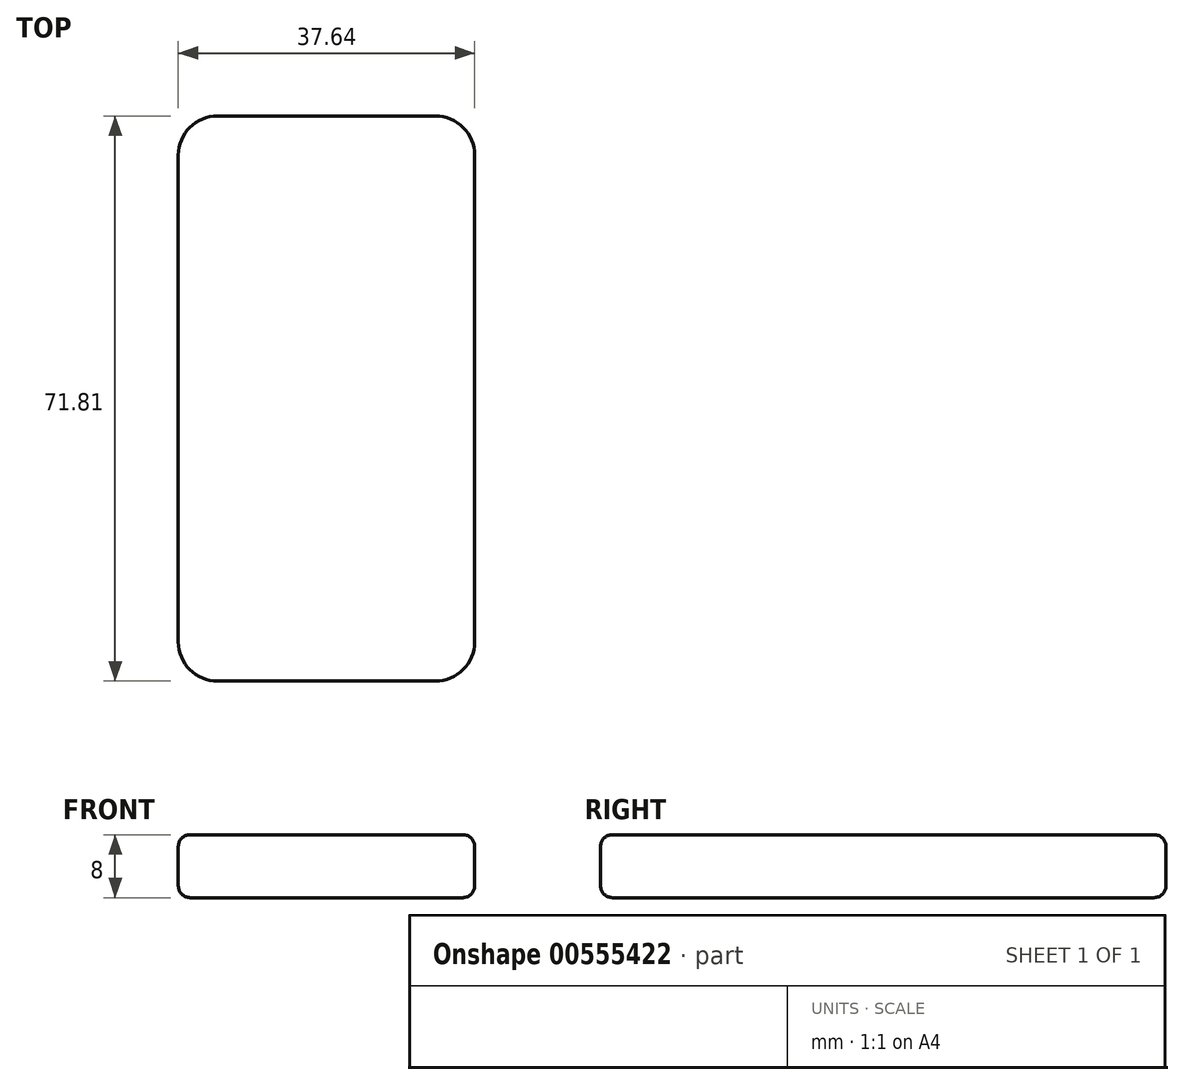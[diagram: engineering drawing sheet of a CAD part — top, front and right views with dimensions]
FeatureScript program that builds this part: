
annotation { "Feature Type Name" : "Feature", "Feature Type Description" : "" }
export const myFeature = defineFeature(function(context is Context, id is Id, definition is map)
    precondition{}
    {
        {
            var Q0;
            Q0=qCreatedBy(makeId("Top.planeOp"),FACE);
            var sketch = newSketch(context, id + "F0", { "sketchPlane" : qUnion([Q0])});
            skLineSegment(sketch, "E0.bottom", {"start": v(-22.69, 34.29) * mm, "end": v(4.95, 34.29) * mm});
            skLineSegment(sketch, "E0.top", {"start": v(-22.69, -37.52) * mm, "end": v(4.95, -37.52) * mm});
            skLineSegment(sketch, "E0.left", {"start": v(-27.69, 29.29) * mm, "end": v(-27.69, -32.52) * mm});
            skLineSegment(sketch, "E0.right", {"start": v(9.95, 29.29) * mm, "end": v(9.95, -32.52) * mm});
            skPoint(sketch, "E1.visualSharp", {"position": v(9.95, 34.29) * mm});
            skArc(sketch, "E1.filletArc", {"start": v(9.95, 29.29) * mm, "mid": v(8.49, 32.82) * mm, "end": v(4.95, 34.29) * mm});
            skPoint(sketch, "E2.visualSharp", {"position": v(-27.69, 34.29) * mm});
            skArc(sketch, "E2.filletArc", {"start": v(-22.69, 34.29) * mm, "mid": v(-26.23, 32.82) * mm, "end": v(-27.69, 29.29) * mm});
            skPoint(sketch, "E3.visualSharp", {"position": v(-27.69, -37.52) * mm});
            skArc(sketch, "E3.filletArc", {"start": v(-27.69, -32.52) * mm, "mid": v(-26.23, -36.06) * mm, "end": v(-22.69, -37.52) * mm});
            skPoint(sketch, "E4.visualSharp", {"position": v(9.95, -37.52) * mm});
            skArc(sketch, "E4.filletArc", {"start": v(4.95, -37.52) * mm, "mid": v(8.49, -36.06) * mm, "end": v(9.95, -32.52) * mm});
            skSolve(sketch);
        }
        {
            var Q0;
            Q0=makeQuery(id+"F0.imprint","IMPRINT",FACE,{"disambiguationData":[TD([[makeQuery(id+"F0.imprint","IMPRINT",EDGE,{"derivedFrom":sQuery(id+"F0.wireOp",EDGE,"E0.bottom")}),-1.0]])]});
            extrude(context, id + "F1", {"entities" : qUnion([Q0]), "depth" : 8 * mm, "offsetDistance" : 25 * mm});
        }
        {
            var Q0;
            Q0=makeQuery(id+"F1.opExtrude","CAP_FACE",FACE,{"disambiguationData":[OSD([sQuery(id+"F0.wireOp",EDGE,"E0.bottom"),sQuery(id+"F0.wireOp",EDGE,"E0.top"),sQuery(id+"F0.wireOp",EDGE,"E0.left"),sQuery(id+"F0.wireOp",EDGE,"E0.right")])],"isStart":false});
            fillet(context, id + "F2", {"entities" : qUnion([Q0]), "radius" : 1.5 * mm, "tangentPropagation" : true, "allowEdgeOverflow" : false});
        }
        {
            var Q0;
            Q0=makeQuery(id+"F1.opExtrude","CAP_FACE",FACE,{"disambiguationData":[OSD([sQuery(id+"F0.wireOp",EDGE,"E0.bottom"),sQuery(id+"F0.wireOp",EDGE,"E0.top"),sQuery(id+"F0.wireOp",EDGE,"E0.left"),sQuery(id+"F0.wireOp",EDGE,"E0.right")])],"isStart":true});
            fillet(context, id + "F3", {"entities" : qUnion([Q0]), "radius" : 1.5 * mm, "tangentPropagation" : true, "allowEdgeOverflow" : false});
        }
    });
